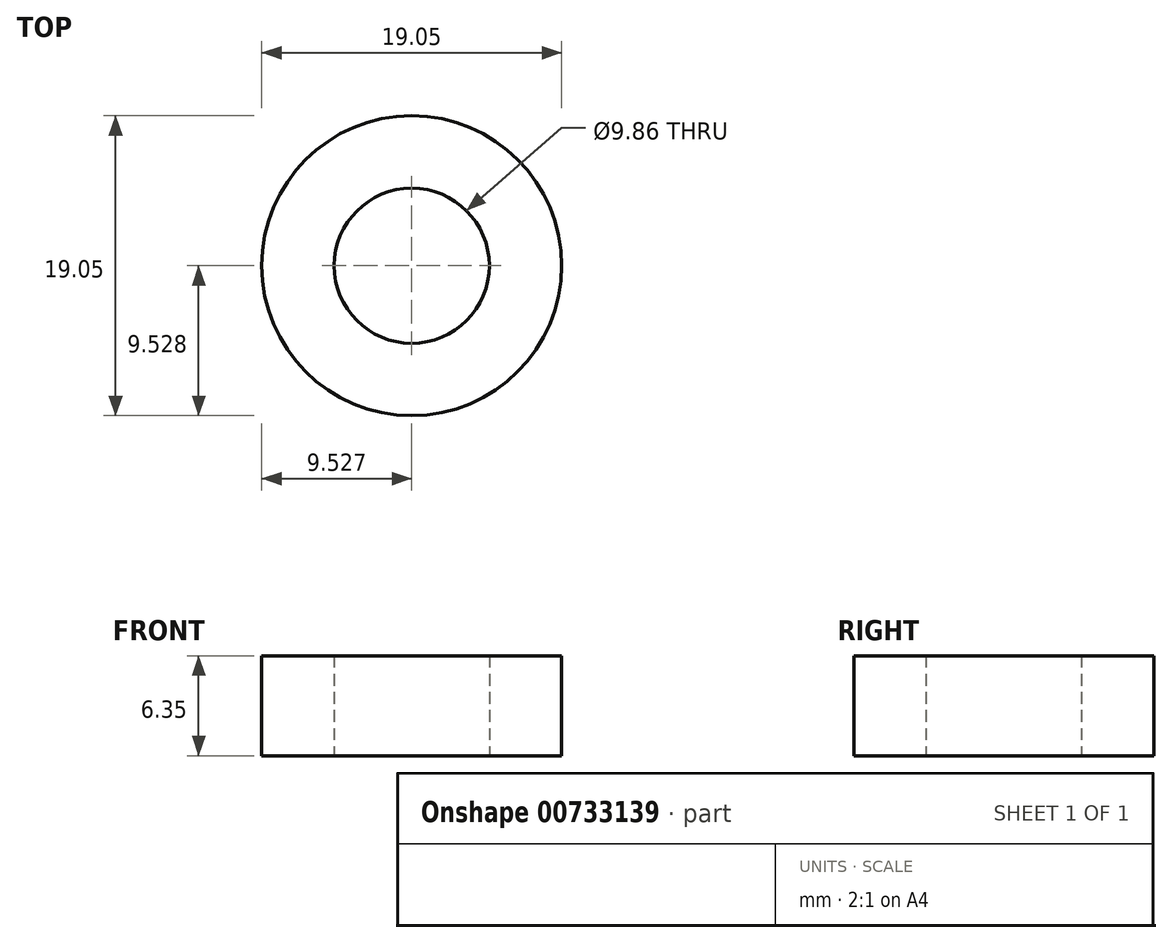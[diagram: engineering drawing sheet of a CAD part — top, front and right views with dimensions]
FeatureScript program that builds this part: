
annotation { "Feature Type Name" : "Feature", "Feature Type Description" : "" }
export const myFeature = defineFeature(function(context is Context, id is Id, definition is map)
    precondition{}
    {
        {
            var Q0;
            Q0=qCreatedBy(makeId("Top.planeOp"),FACE);
            var sketch = newSketch(context, id + "F0", { "sketchPlane" : qUnion([Q0])});
            skCircle(sketch, "E0", {"center": v(-6.11, 6.58) * mm, "radius": 9.53 * mm});
            skCircle(sketch, "E1", {"center": v(-6.11, 6.58) * mm, "radius": 4.93 * mm});
            skSolve(sketch);
        }
        {
            var Q0;
            Q0 = qSketchRegion(id + "F0", true);
            extrude(context, id + "F1", {"entities" : qUnion([Q0]), "depth" : 6.35 * mm, "offsetDistance" : 25.4 * mm});
        }
    });
